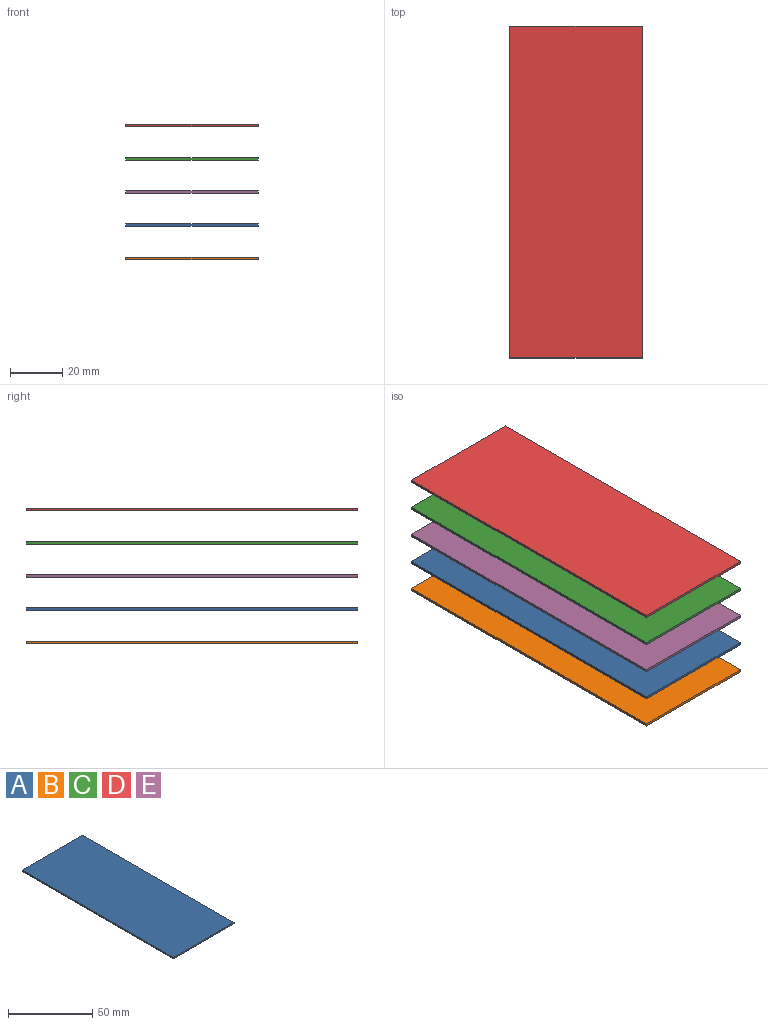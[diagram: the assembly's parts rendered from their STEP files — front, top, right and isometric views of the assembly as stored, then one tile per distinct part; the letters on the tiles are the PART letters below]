
ASSEMBLY  parts=5 mates=8
PART A: 6 faces, bbox 50.8x127x1 mm
  f0: plane 127x1mm, normal (-1,0,0), area 127mm2, adj f1,f3,f4,f5
  f1: plane 50.8x1mm, normal (0,-1,0), area 50.8mm2, adj f0,f2,f4,f5
  f2: plane 127x1mm, normal (1,0,0), area 127mm2, adj f1,f3,f4,f5
  f3: plane 50.8x1mm, normal (0,1,0), area 50.8mm2, adj f0,f2,f4,f5
  f4: plane 127x50.8mm, normal (0,0,1), area 6451.6mm2, adj f0,f1,f2,f3
  f5: plane 127x50.8mm, normal (0,0,-1), area 6451.6mm2, adj f0,f1,f2,f3
PART B: same geometry as A
PART C: same geometry as A
PART D: same geometry as A
PART E: same geometry as A
PLACE A t=(0,0,12.7)mm
PLACE B at identity fixed
PLACE C t=(0,0,38.1)mm
PLACE D t=(0,0,50.8)mm
PLACE E t=(0,0,25.4)mm
MATE planar E.f2 <-> B.f2  axis (1,0,0) through (25.4,0,25.9)mm
MATE planar D.f3 <-> B.f3  axis (0,1,0) through (0,63.5,51.3)mm
MATE planar B.f2 <-> A.f2  axis (1,0,0) through (25.4,0,0.5)mm
MATE planar C.f2 <-> B.f2  axis (1,0,0) through (25.4,0,38.6)mm
MATE planar D.f2 <-> B.f2  axis (1,0,0) through (25.4,0,51.3)mm
MATE planar E.f3 <-> B.f3  axis (0,1,0) through (0,63.5,25.9)mm
MATE planar A.f3 <-> B.f3  axis (0,1,0) through (0,63.5,13.2)mm
MATE planar C.f3 <-> B.f3  axis (0,1,0) through (0,63.5,38.6)mm
